annotation { "Feature Type Name" : "Feature", "Feature Type Description" : "" }
export const myFeature = defineFeature(function(context is Context, id is Id, definition is map)
    precondition{}
    {
        {
            var Q0;
            Q0=qCreatedBy(makeId("Top.planeOp"),FACE);
            var sketch = newSketch(context, id + "F0", { "sketchPlane" : qUnion([Q0])});
            skLineSegment(sketch, "E0", {"start": v(-243.27, 457.91) * mm, "end": v(479.25, 457.91) * mm});
            skLineSegment(sketch, "E1", {"start": v(479.25, 457.91) * mm, "end": v(479.25, 344.16) * mm});
            skLineSegment(sketch, "E2", {"start": v(479.25, 344.16) * mm, "end": v(-243.27, 344.16) * mm});
            skLineSegment(sketch, "E3", {"start": v(-243.27, 344.16) * mm, "end": v(-243.27, 457.91) * mm});
            skLineSegment(sketch, "E4", {"start": v(-341.47, 526.61) * mm, "end": v(456.79, 526.61) * mm});
            skLineSegment(sketch, "E5", {"start": v(-243.27, 344.16) * mm, "end": v(538.97, 119.85) * mm, "construction": true});
            skLineSegment(sketch, "E6", {"start": v(1142.93, 271.38) * mm, "end": v(2276.4, 740.87) * mm});
            skLineSegment(sketch, "E7", {"start": v(2276.4, 740.87) * mm, "end": v(2092.26, 1185.44) * mm});
            skLineSegment(sketch, "E8", {"start": v(2092.26, 1185.44) * mm, "end": v(958.79, 715.94) * mm});
            skLineSegment(sketch, "E9", {"start": v(958.79, 715.94) * mm, "end": v(1142.93, 271.38) * mm});
            skLineSegment(sketch, "E10", {"start": v(1142.93, 271.38) * mm, "end": v(2384.95, 271.38) * mm, "construction": true});
            skSolve(sketch);
        }
        {
            var Q0;
            Q0=makeQuery(id+"F0.imprint","IMPRINT",FACE,{"disambiguationData":[TD([[makeQuery(id+"F0.imprint","IMPRINT",EDGE,{"derivedFrom":sQuery(id+"F0.wireOp",EDGE,"E6")}),1.0]])]});
            var Q1;
            Q1=sQuery(id+"F0.wireOp",EDGE,"E10");
            revolve(context, id + "F1", {"surfaceOperationType" : NewSurfaceOperationType.NEW, "entities" : qUnion([Q0]), "axis" : qUnion([Q1]), "revolveType" : RevolveType.SYMMETRIC, "angle" : 135 * degree});
        }
        {
            var Q0;
            Q0=makeQuery(id+"F1.opRevolve","SWEPT_EDGE",EDGE,{"disambiguationData":[OSD([sQuery(id+"F0.wireOp",EDGE,"E6"),sQuery(id+"F0.wireOp",EDGE,"E7")])]});
            var Q1;
            Q1=makeQuery(id+"F1.opRevolve","SWEPT_EDGE",EDGE,{"disambiguationData":[OSD([sQuery(id+"F0.wireOp",EDGE,"E7"),sQuery(id+"F0.wireOp",EDGE,"E8")])]});
            var Q2;
            Q2=makeQuery(id+"F1.opRevolve","CAP_EDGE",EDGE,{"disambiguationData":[OSD([sQuery(id+"F0.wireOp",EDGE,"E7")])],"isStart":true});
            var Q3;
            Q3=makeQuery(id+"F1.opRevolve","CAP_EDGE",EDGE,{"disambiguationData":[OSD([sQuery(id+"F0.wireOp",EDGE,"E8")])],"isStart":false});
            var Q4;
            Q4=makeQuery(id+"F1.opRevolve","CAP_EDGE",EDGE,{"disambiguationData":[OSD([sQuery(id+"F0.wireOp",EDGE,"E7")])],"isStart":false});
            var Q5;
            Q5=makeQuery(id+"F1.opRevolve","CAP_EDGE",EDGE,{"disambiguationData":[OSD([sQuery(id+"F0.wireOp",EDGE,"E6")])],"isStart":true});
            var Q6;
            Q6=makeQuery(id+"F1.opRevolve","CAP_EDGE",EDGE,{"disambiguationData":[OSD([sQuery(id+"F0.wireOp",EDGE,"E6")])],"isStart":false});
            var Q7;
            Q7=makeQuery(id+"F1.opRevolve","CAP_EDGE",EDGE,{"disambiguationData":[OSD([sQuery(id+"F0.wireOp",EDGE,"E8")])],"isStart":true});
            fillet(context, id + "F2", {"entities" : qUnion([Q0, Q1, Q2, Q3, Q4, Q5, Q6, Q7]), "radius" : 30.48 * mm, "tangentPropagation" : true, "allowEdgeOverflow" : false});
        }
        {
            var Q0;
            Q0=qCreatedBy(makeId("Top.planeOp"),FACE);
            var sketch = newSketch(context, id + "F3", { "sketchPlane" : qUnion([Q0])});
            skText(sketch, "E11", { "text": "Big Red Thing Up my ...\nFeels SOOO  GOOOOD \n        &\nThe Strokin\' is \n    Fantastical!", "fontName": "RobotoSlab-Regular.ttf"});
            const initialGuessF3  = {"E11": [-8.47497, -3.9931, 1, 0, 6.01552]};
            skSetInitialGuess(sketch, initialGuessF3);
            skSolve(sketch);
        }
        {
            var Q0;
            Q0 = qSketchRegion(id + "F3", true);
            extrude(context, id + "F4", {"entities" : qUnion([Q0]), "depth" : 25.4 * mm, "offsetDistance" : 25.4 * mm});
        }
    });